# Revit family: Door_Sliding_Vinyl_Harvey-3Panel
name_source: partatom
category: Doors
units: mm (PartAtom-declared; Revit-internal decimal feet)

## family parameters
Always vertical = Yes
Classification Number = 23.30.10.17.11
Cut with Voids When Loaded = No
Host = Wall
Room Calculation Point = No
Shared = No

## types (2) — shared parameters
AAMA Conformance = SD-R35 (DP35)
Analytic Construction = <None>
Assembly Code = B2030100
CAD Details = https://www.arcat.com
Define Thermal Properties by = Schematic Type
Door Height = 6' - 5 5/8"
E283_Air-Infiltration = As Specified in 08 53 13
E330_Structural-Test-Pressure = As Specified in 08 53 13
E547_Water-Resistance = As Specified in 08 53 13
F588_Forced-Entry = Type B; Grade 10
Fire Rating = As Specified in 08 53 13
Frame Material = ARCAT - Vinyl - PVC - 0.070" - White
Function = Interior
Glass Thickness = 0' - 0 7/8"
Glass Type = ARCAT - Glass - Laminated - Clear
Hardware Finish = ARCAT - Vinyl - PVC - 0.070" - White
Height = 6' - 7 3/4"
Keynote = 08 53 13
LH = Yes
Manufacturer = Harvey Building Products
Operation = As Specified in 08 53 13
Product Page URL = https://www.arcat.com
RH = No
RO Spacing = 0' - 0 5/8"
Rough Height = 6' - 8 3/8"
Sound Transmission Class (STC) = 29
Specification = https://www.arcat.com
URL = https://harveywindows.com
Wall Closure = By host

## per-type parameters (varying)
| type | Description | Door Width | Rough Width | Width |
| PD 12068-3 | Harvey BP - PD 12068-3 Sliding Patio Door | 4' - 0 31/32" | 12' - 1" | 11' - 11 3/4" |
| PD 9068-3 | Harvey BP - PD 9068-3 Sliding Patio Door | 3' - 0 31/32" | 9' - 1" | 8' - 11 3/4" |

note: column(s) folded — value = type name in every type: Model

## geometry (parser evidence)
native form markers: Blend x8, Sweep x8
no freeform markers — native parametric forms only
